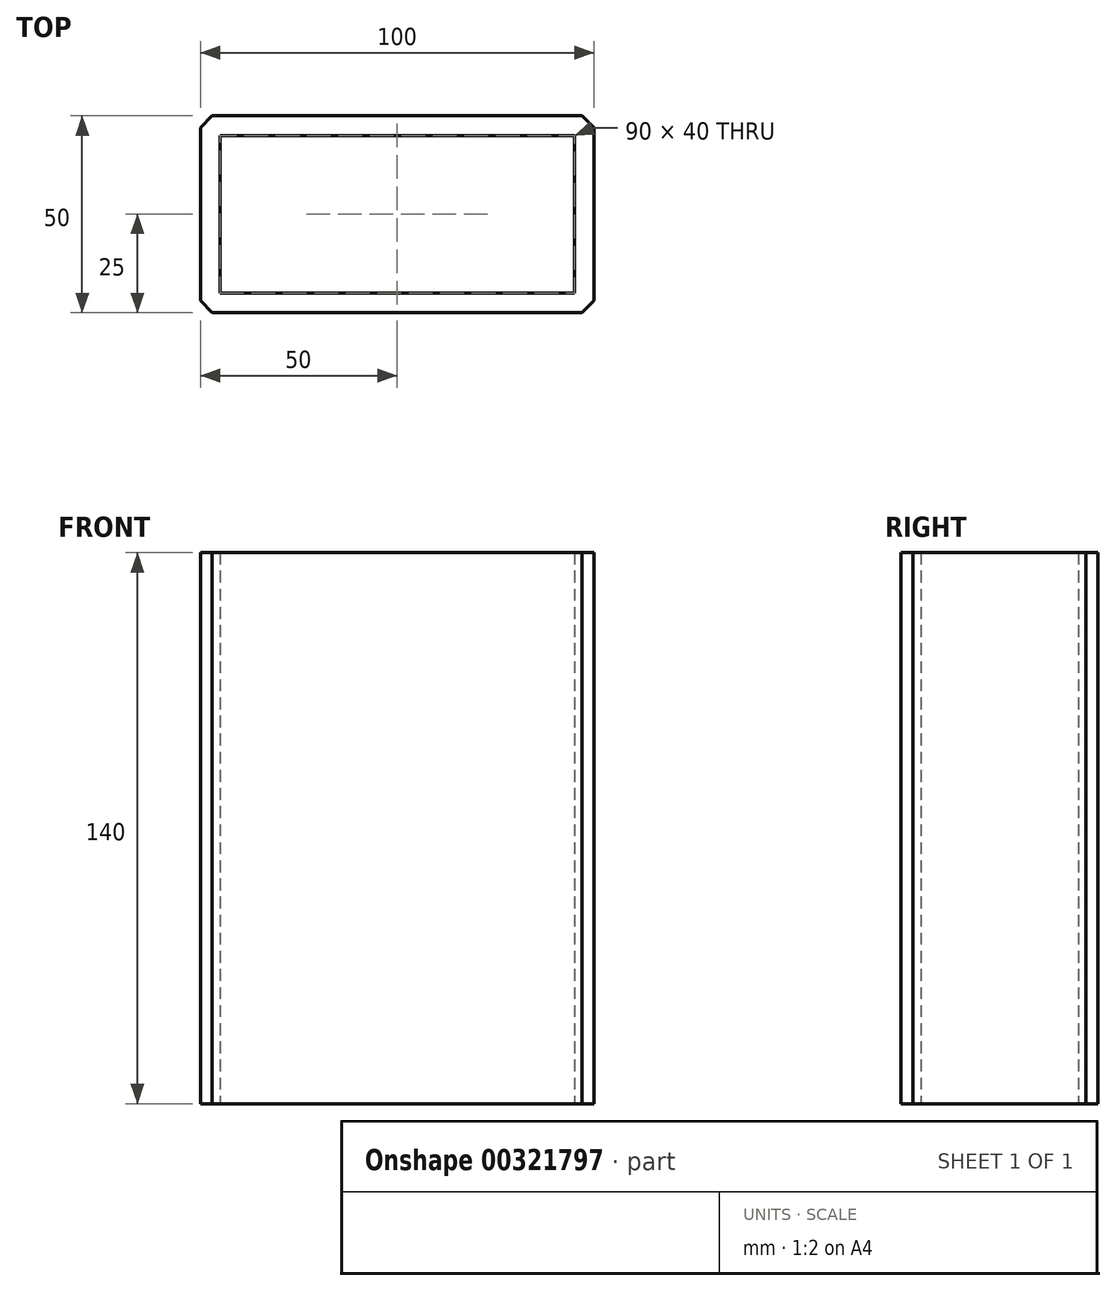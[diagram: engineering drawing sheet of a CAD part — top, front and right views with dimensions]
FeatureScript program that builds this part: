
annotation { "Feature Type Name" : "Feature", "Feature Type Description" : "" }
export const myFeature = defineFeature(function(context is Context, id is Id, definition is map)
    precondition{}
    {
        {
            var Q0;
            Q0=qCreatedBy(makeId("Top.planeOp"),FACE);
            var sketch = newSketch(context, id + "F0", { "sketchPlane" : qUnion([Q0])});
            skLineSegment(sketch, "E0.bottom", {"start": v(-50, 25) * mm, "end": v(50, 25) * mm});
            skLineSegment(sketch, "E0.top", {"start": v(-50, -25) * mm, "end": v(50, -25) * mm});
            skLineSegment(sketch, "E0.left", {"start": v(-50, 25) * mm, "end": v(-50, -25) * mm});
            skLineSegment(sketch, "E0.right", {"start": v(50, 25) * mm, "end": v(50, -25) * mm});
            skLineSegment(sketch, "E1.0", {"start": v(-45, 20) * mm, "end": v(-45, -20) * mm});
            skLineSegment(sketch, "E1.1", {"start": v(-45, 20) * mm, "end": v(45, 20) * mm});
            skLineSegment(sketch, "E1.2", {"start": v(45, 20) * mm, "end": v(45, -20) * mm});
            skLineSegment(sketch, "E1.3", {"start": v(-45, -20) * mm, "end": v(45, -20) * mm});
            skSolve(sketch);
        }
        {
            var Q0;
            Q0=makeQuery(id+"F0.imprint","IMPRINT",FACE,{"disambiguationData":[TD([[makeQuery(id+"F0.imprint","IMPRINT",EDGE,{"derivedFrom":sQuery(id+"F0.wireOp",EDGE,"E0.bottom")}),-1.0]])]});
            extrude(context, id + "F1", {"entities" : qUnion([Q0]), "depth" : 140 * mm});
        }
        {
            var Q0;
            Q0=makeQuery(id+"F1.opExtrude","SWEPT_EDGE",EDGE,{"disambiguationData":[OSD([sQuery(id+"F0.wireOp",EDGE,"E0.top"),sQuery(id+"F0.wireOp",EDGE,"E0.right")])]});
            var Q1;
            Q1=makeQuery(id+"F1.opExtrude","SWEPT_EDGE",EDGE,{"disambiguationData":[OSD([sQuery(id+"F0.wireOp",EDGE,"E0.bottom"),sQuery(id+"F0.wireOp",EDGE,"E0.right")])]});
            var Q2;
            Q2=makeQuery(id+"F1.opExtrude","SWEPT_EDGE",EDGE,{"disambiguationData":[OSD([sQuery(id+"F0.wireOp",EDGE,"E0.top"),sQuery(id+"F0.wireOp",EDGE,"E0.left")])]});
            var Q3;
            Q3=makeQuery(id+"F1.opExtrude","SWEPT_EDGE",EDGE,{"disambiguationData":[OSD([sQuery(id+"F0.wireOp",EDGE,"E0.bottom"),sQuery(id+"F0.wireOp",EDGE,"E0.left")])]});
            chamfer(context, id + "F2", {"entities" : qUnion([Q0, Q1, Q2, Q3]), "width" : 3 * mm, "tangentPropagation" : true});
        }
    });
